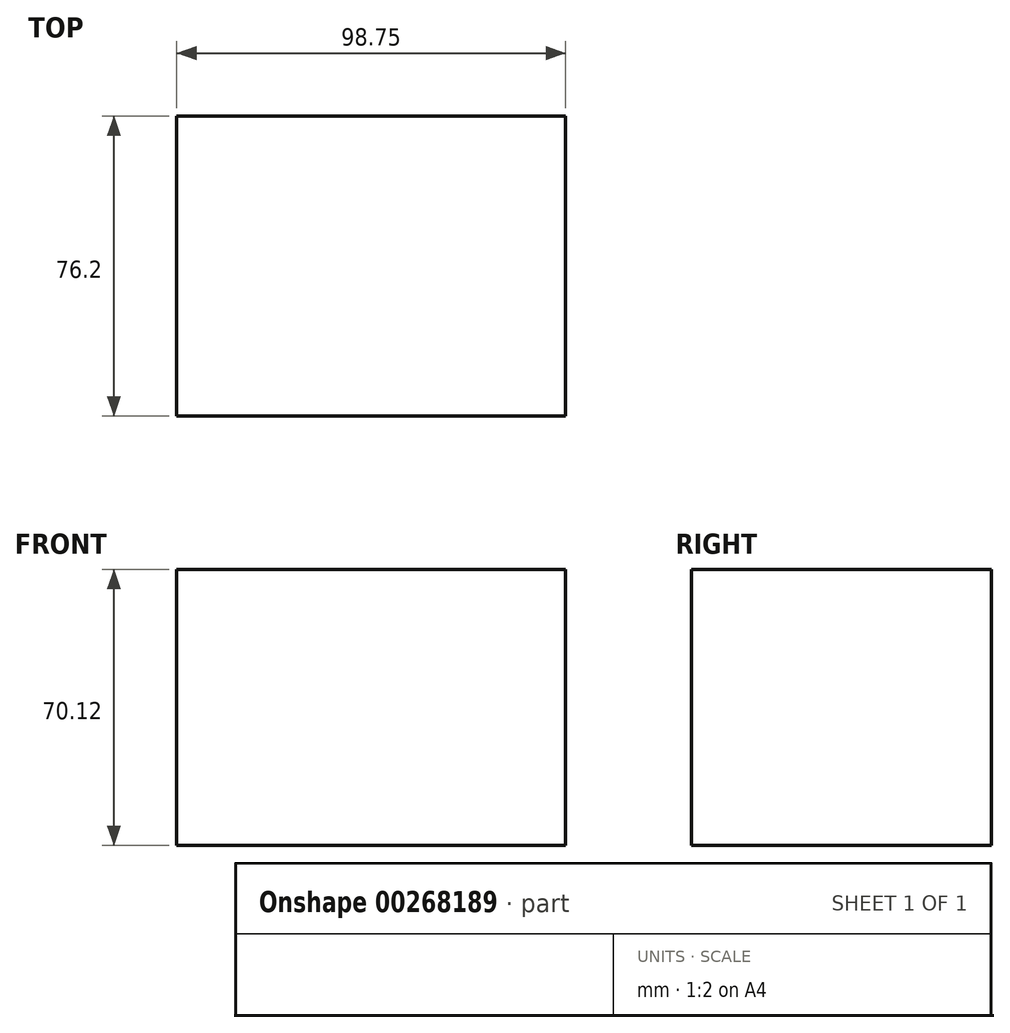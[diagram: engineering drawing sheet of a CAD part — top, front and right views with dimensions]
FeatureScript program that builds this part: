
annotation { "Feature Type Name" : "Feature", "Feature Type Description" : "" }
export const myFeature = defineFeature(function(context is Context, id is Id, definition is map)
    precondition{}
    {
        {
            var Q0;
            Q0=qCreatedBy(makeId("Front.planeOp"),FACE);
            var sketch = newSketch(context, id + "F0", { "sketchPlane" : qUnion([Q0])});
            skLineSegment(sketch, "E0.bottom", {"start": v(52.49, 51.45) * mm, "end": v(-46.26, 51.45) * mm});
            skLineSegment(sketch, "E0.top", {"start": v(52.49, -18.67) * mm, "end": v(-46.26, -18.67) * mm});
            skLineSegment(sketch, "E0.left", {"start": v(52.49, 51.45) * mm, "end": v(52.49, -18.67) * mm});
            skLineSegment(sketch, "E0.right", {"start": v(-46.26, 51.45) * mm, "end": v(-46.26, -18.67) * mm});
            skSolve(sketch);
        }
        {
            var Q0;
            Q0=makeQuery(id+"F0.imprint","IMPRINT",FACE,{"disambiguationData":[TD([[makeQuery(id+"F0.imprint","IMPRINT",EDGE,{"derivedFrom":sQuery(id+"F0.wireOp",EDGE,"E0.bottom")}),1.0]])]});
            var Q1;
            Q1 = qSketchRegion(id + "F0", true);
            extrude(context, id + "F1", {"entities" : qUnion([Q0, Q1]), "depth" : 76.2 * mm});
        }
    });
